# Revit family: Kemper - 1602G08000
name_source: partatom
category: Rohrzubehör
units: mm (PartAtom-declared; Revit-internal decimal feet)

## family parameters
Arbeitsebenenbasiert = Nein
Beim Laden mit Abzugskörper schneiden = Nein
Bemaßung runder Anschluss = Durchmesser verwenden
Gemeinsam genutzt = Nein
Immer vertikal = Ja
OmniClass-Nummer = 23.65.55.14
OmniClass-Titel = Valves for Liquid Services
Teiletyp = Ventil - Zerlegung in

## types (1)
- DN 80
    AssetType = Fixed
    Datanorm = 1602G08000
    DurationUnit = Years
    Flow = 0
    Generation ID = Kemper - 1602G08000
    Manufacturer = Kemper
    Material = gunmetal
    Model = 160 2G, combined stop and antipollution check valve, with plugged drain port, union thread
    Modelnumber = 1602G08000
    Shape = Valve
    Size DN = 80
    Tmax, Control °C = 0
    Tmin, Control °C = 0
    WarrantyDurationUnit = Years
    collision height = 392 mm
    collision length = 409 mm
    collision volume = 408.999972895467 x 120 x 392.164972895467
    collision width = 120 mm
    design = pass
    kVs-Value = 130
    max. differential pressure = 1000
    perm. operating Temperature °C = 100
    perm. operating pressure Bar = 16
    productgroup = Safety valves
    type = Sicherungsarmatur
    type of connection = male thread
    typedescription = Safety valves, 160 2G, combined stop and antipollution check valve, with plugged drain port, union thread
    valvetype = Rückflussverhinderer
